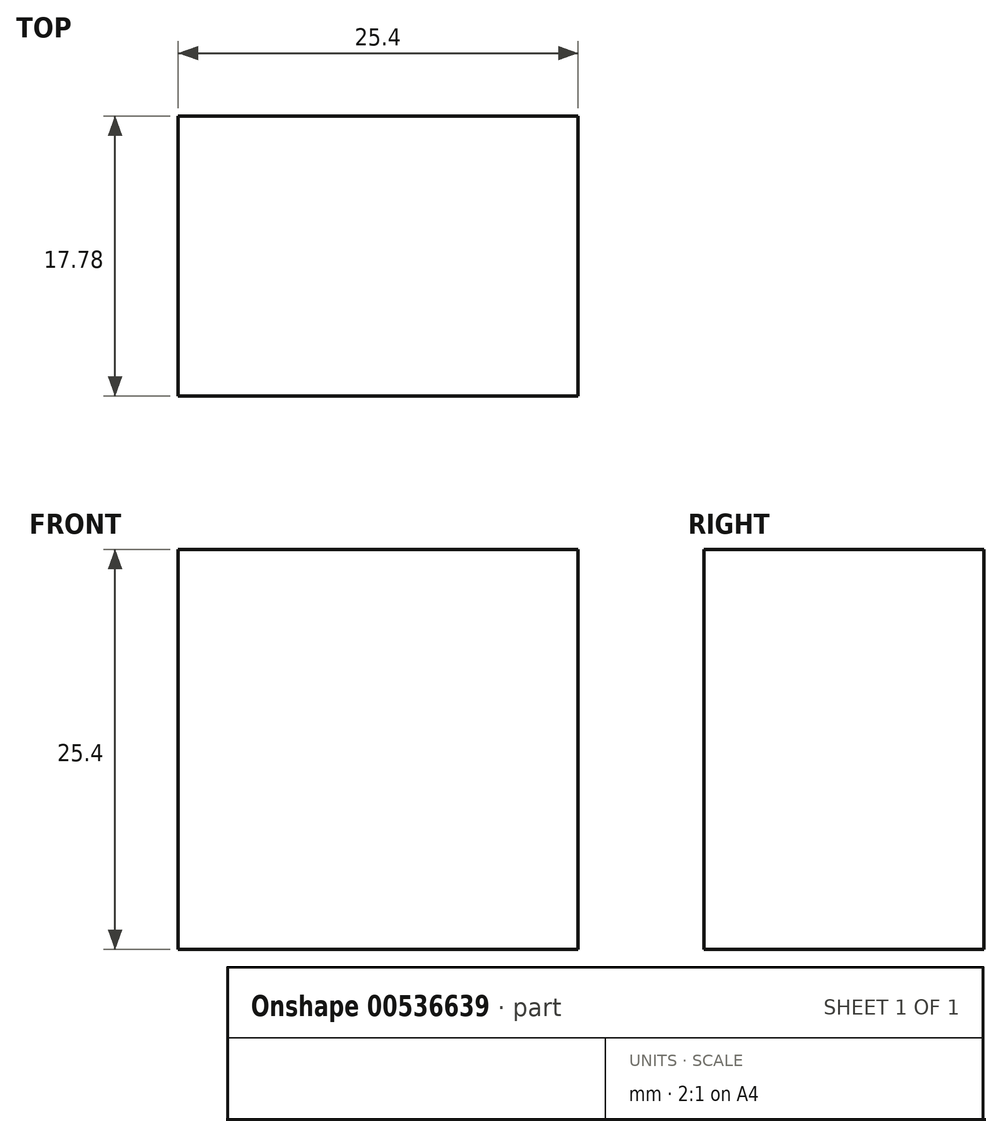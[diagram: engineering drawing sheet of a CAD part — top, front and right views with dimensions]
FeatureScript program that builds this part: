
annotation { "Feature Type Name" : "Feature", "Feature Type Description" : "" }
export const myFeature = defineFeature(function(context is Context, id is Id, definition is map)
    precondition{}
    {
        {
            var Q0;
            Q0=qCreatedBy(makeId("Front.planeOp"),FACE);
            var sketch = newSketch(context, id + "F0", { "sketchPlane" : qUnion([Q0])});
            skLineSegment(sketch, "E0.bottom", {"start": v(-9.1, -5.16) * mm, "end": v(16.3, -5.16) * mm});
            skLineSegment(sketch, "E0.top", {"start": v(-9.1, -30.56) * mm, "end": v(16.3, -30.56) * mm});
            skLineSegment(sketch, "E0.left", {"start": v(-9.1, -5.16) * mm, "end": v(-9.1, -30.56) * mm});
            skLineSegment(sketch, "E0.right", {"start": v(16.3, -5.16) * mm, "end": v(16.3, -30.56) * mm});
            skSolve(sketch);
        }
        {
            var Q0;
            Q0 = qSketchRegion(id + "F0", true);
            extrude(context, id + "F1", {"entities" : qUnion([Q0]), "depth" : 17.78 * mm, "offsetDistance" : 25.4 * mm});
        }
    });
